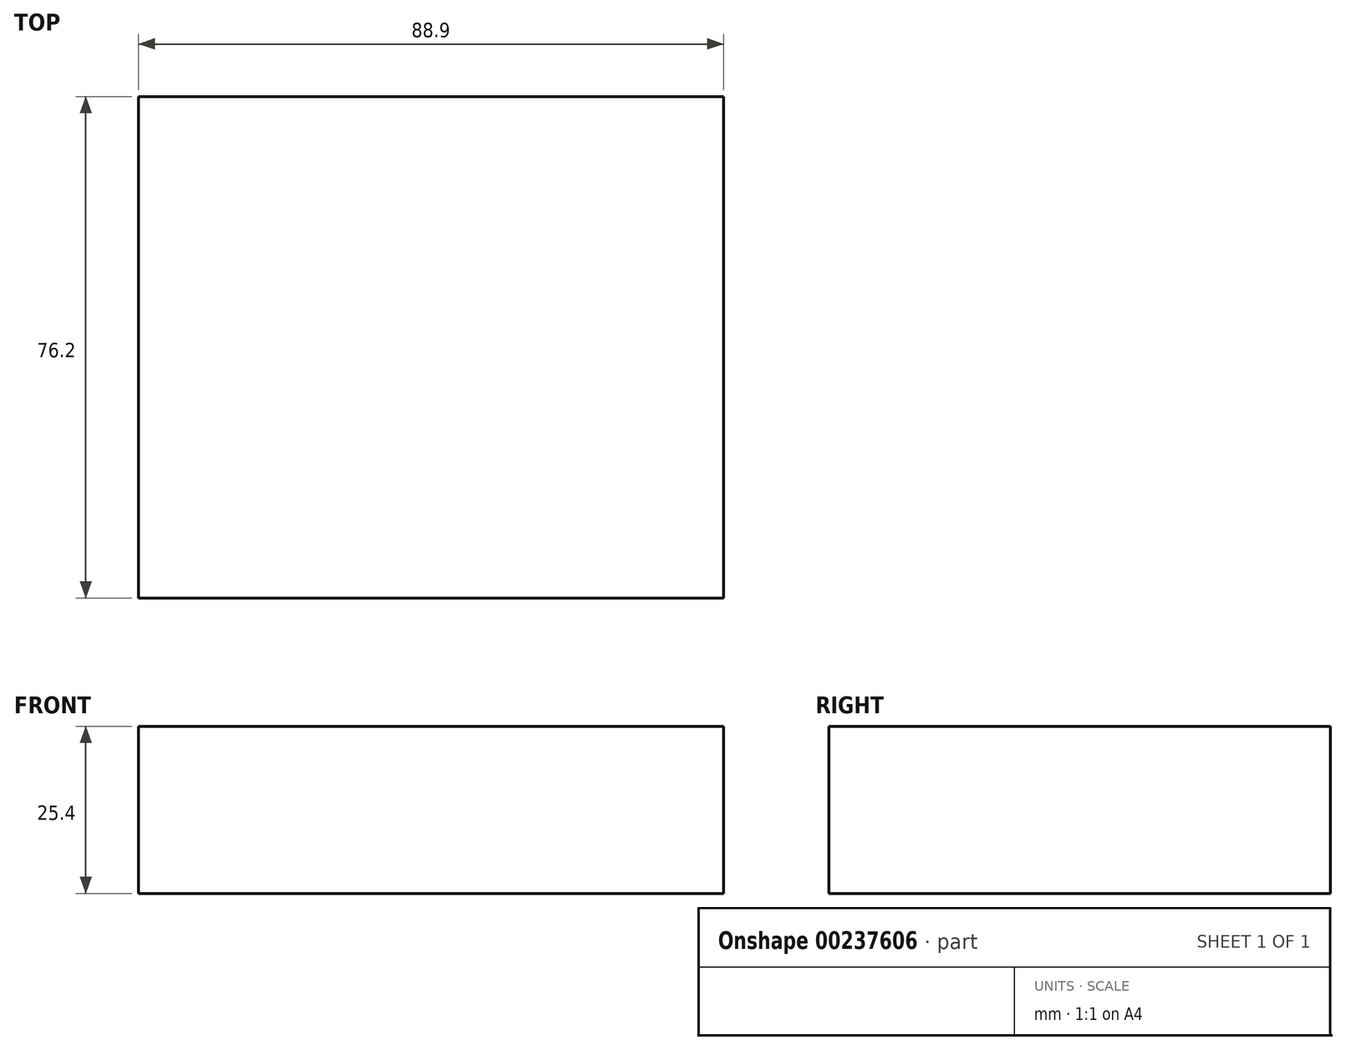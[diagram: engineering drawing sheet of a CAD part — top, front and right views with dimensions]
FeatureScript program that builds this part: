
annotation { "Feature Type Name" : "Feature", "Feature Type Description" : "" }
export const myFeature = defineFeature(function(context is Context, id is Id, definition is map)
    precondition{}
    {
        {
            var Q0;
            Q0=qCreatedBy(makeId("Top.planeOp"),FACE);
            var sketch = newSketch(context, id + "F0", { "sketchPlane" : qUnion([Q0])});
            skLineSegment(sketch, "E0.bottom", {"start": v(44.45, -38.1) * mm, "end": v(-44.45, -38.1) * mm});
            skLineSegment(sketch, "E0.top", {"start": v(44.45, 38.1) * mm, "end": v(-44.45, 38.1) * mm});
            skLineSegment(sketch, "E0.left", {"start": v(44.45, -38.1) * mm, "end": v(44.45, 38.1) * mm});
            skLineSegment(sketch, "E0.right", {"start": v(-44.45, -38.1) * mm, "end": v(-44.45, 38.1) * mm});
            skPoint(sketch, "E0.middle", {"position": v(0, 0) * mm});
            skSolve(sketch);
        }
        {
            var Q0;
            Q0 = qSketchRegion(id + "F0", true);
            var Q1;
            Q1=makeQuery(id+"F0.imprint","IMPRINT",FACE,{"disambiguationData":[TD([[makeQuery(id+"F0.imprint","IMPRINT",EDGE,{"derivedFrom":sQuery(id+"F0.wireOp",EDGE,"E0.bottom")}),-1.0]])]});
            extrude(context, id + "F1", {"entities" : qUnion([Q0, Q1]), "depth" : 25.4 * mm});
        }
    });
